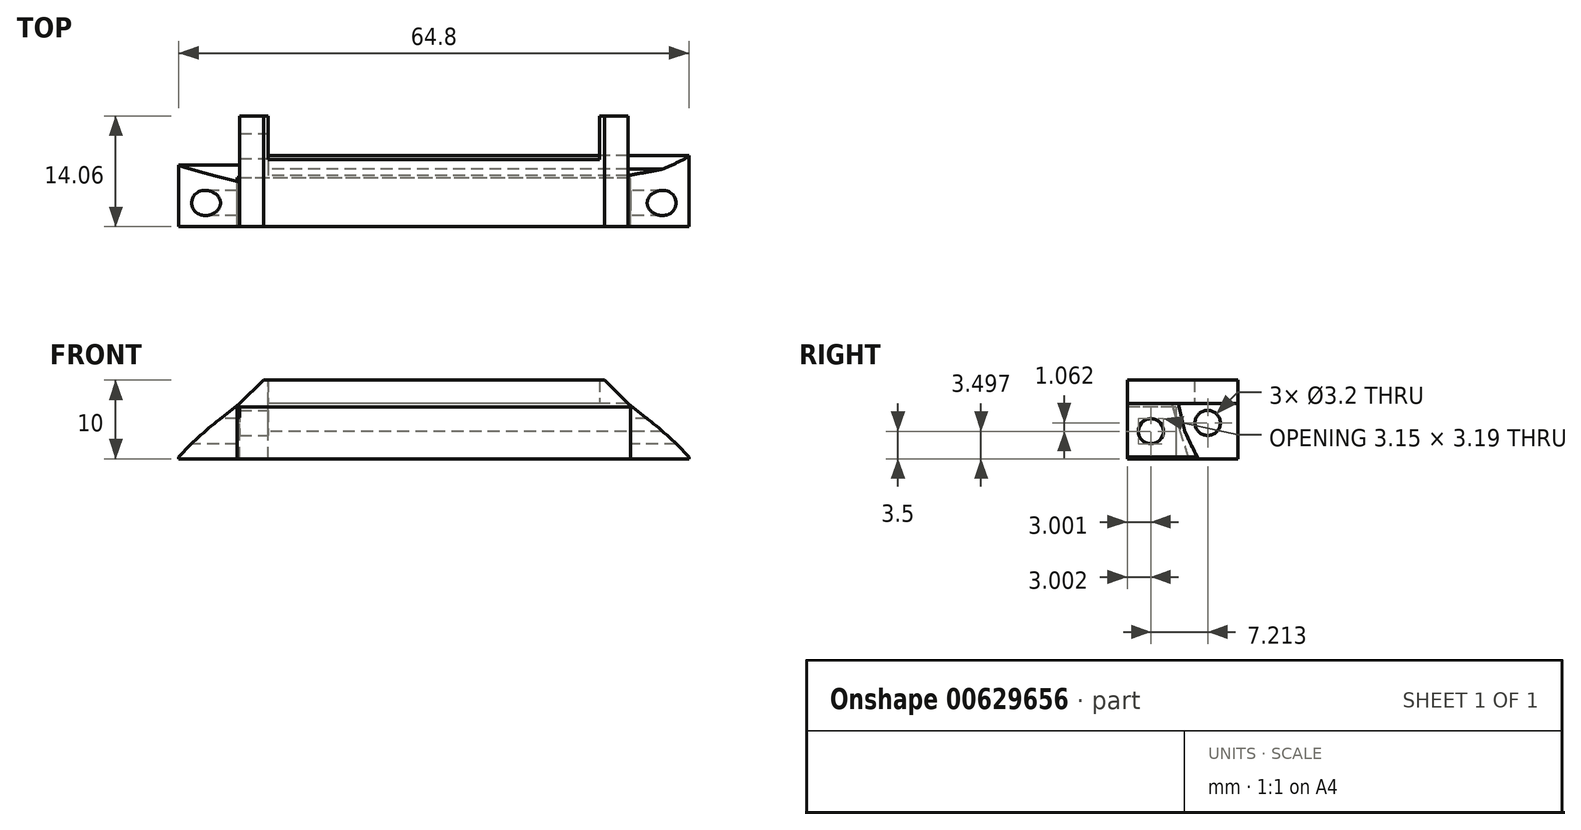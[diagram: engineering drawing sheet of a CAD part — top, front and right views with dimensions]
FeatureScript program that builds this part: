
annotation { "Feature Type Name" : "Feature", "Feature Type Description" : "" }
export const myFeature = defineFeature(function(context is Context, id is Id, definition is map)
    precondition{}
    {
        {
            var Q0;
            Q0=qCreatedBy(makeId("Right.planeOp"),FACE);
            cPlane(context, id + "F0", {"entities" : qUnion([Q0]), "cplaneType" : CPlaneType.OFFSET, "offset" : 40 * mm, "oppositeDirection" : true, "width" : 150 * mm, "height" : 150 * mm});
        }
        {
            var Q0;
            Q0=qCreatedBy(id+"F0.planeOp",FACE);
            var sketch = newSketch(context, id + "F1", { "sketchPlane" : qUnion([Q0])});
            skLineSegment(sketch, "E0.0", {"start": v(-62.06, 47) * mm, "end": v(-55.56, 47) * mm});
            skLineSegment(sketch, "E1.0", {"start": v(-62.06, 40) * mm, "end": v(-53.06, 40) * mm});
            skLineSegment(sketch, "E2", {"start": v(-62.06, 47) * mm, "end": v(-62.06, 40) * mm});
            skCircle(sketch, "E3", {"center": v(-59.06, 43.5) * mm, "radius": 1.6 * mm});
            skArc(sketch, "E4.0", {"start": v(-55.56, 47) * mm, "mid": v(-55.17, 45.25) * mm, "end": v(-54.76, 43.5) * mm});
            skArc(sketch, "E5.0", {"start": v(-53.06, 40) * mm, "mid": v(-53.92, 41.74) * mm, "end": v(-54.76, 43.5) * mm});
            skCircle(sketch, "E6", {"center": v(-59.06, 43.5) * mm, "radius": 3.25 * mm, "construction": true});
            skSolve(sketch);
        }
        {
            var Q0;
            Q0=qSketchRegion(id+"F1",true);
            extrude(context, id + "F2", {"entities" : qUnion([Q0]), "depth" : 33 * mm, "hasSecondDirection" : true, "secondDirectionOppositeDirection" : true, "secondDirectionDepth" : 33 * mm});
        }
        {
            var Q0;
            Q0=qCreatedBy(makeId("Front.planeOp"),FACE);
            var sketch = newSketch(context, id + "F3", { "sketchPlane" : qUnion([Q0])});
            skLineSegment(sketch, "E7", {"start": v(-40, 73.73) * mm, "end": v(-40, 20.27) * mm, "construction": true});
            skLineSegment(sketch, "E8.MirrorCS", {"start": v(-67.23, 45) * mm, "end": v(-64.65, 47) * mm});
            skArc(sketch, "E9.MirrorCS", {"start": v(-72.4, 40.2) * mm, "mid": v(-69.92, 42.72) * mm, "end": v(-67.23, 45) * mm});
            skLineSegment(sketch, "E10", {"start": v(-64.65, 47) * mm, "end": v(-77.52, 47) * mm});
            skLineSegment(sketch, "E11", {"start": v(-77.52, 47) * mm, "end": v(-77.52, 39.44) * mm});
            skLineSegment(sketch, "E12", {"start": v(-77.52, 39.44) * mm, "end": v(-72.4, 39.44) * mm});
            skLineSegment(sketch, "E13", {"start": v(-72.4, 39.44) * mm, "end": v(-72.4, 40.2) * mm});
            skLineSegment(sketch, "E14.MirrorCS", {"start": v(-7.6, 39.44) * mm, "end": v(-7.6, 40.2) * mm});
            skLineSegment(sketch, "E15.MirrorCS", {"start": v(-12.77, 45) * mm, "end": v(-15.35, 47) * mm});
            skLineSegment(sketch, "E16.MirrorCS", {"start": v(-2.48, 39.44) * mm, "end": v(-7.6, 39.44) * mm});
            skLineSegment(sketch, "E17.MirrorCS", {"start": v(-2.48, 47) * mm, "end": v(-2.48, 39.44) * mm});
            skArc(sketch, "E18.MirrorCS", {"start": v(-7.6, 40.2) * mm, "mid": v(-10.08, 42.72) * mm, "end": v(-12.77, 45) * mm});
            skLineSegment(sketch, "E19.MirrorCS", {"start": v(-15.35, 47) * mm, "end": v(-2.48, 47) * mm});
            skSolve(sketch);
        }
        {
            var Q0;
            Q0=qSketchRegion(id+"F3",true);
            extrude(context, id + "F4", {"entities" : qUnion([Q0]), "operationType" : NewBodyOperationType.REMOVE, "endBound" : BoundingType.THROUGH_ALL, "depth" : 25 * mm});
        }
        {
            var Q0;
            Q0=qCreatedBy(makeId("Front.planeOp"),FACE);
            cPlane(context, id + "F5", {"entities" : qUnion([Q0]), "cplaneType" : CPlaneType.OFFSET, "offset" : 48 * mm, "width" : 150 * mm, "height" : 150 * mm});
        }
        {
            var Q0;
            Q0=qCreatedBy(id+"F5.planeOp",FACE);
            var sketch = newSketch(context, id + "F6", { "sketchPlane" : qUnion([Q0])});
            skCircle(sketch, "E20", {"center": v(-62.85, 44.9) * mm, "radius": 1.8 * mm, "construction": true});
            skLineSegment(sketch, "E21", {"start": v(-64.65, 44.9) * mm, "end": v(-64.65, 47) * mm});
            skLineSegment(sketch, "E22", {"start": v(-64.65, 44.9) * mm, "end": v(-64.65, 40) * mm});
            skLineSegment(sketch, "E23", {"start": v(-62.85, 50.35) * mm, "end": v(-62.85, 37.67) * mm, "construction": true});
            skLineSegment(sketch, "E24.MirrorCS", {"start": v(-61.05, 44.9) * mm, "end": v(-61.05, 47) * mm});
            skLineSegment(sketch, "E25.MirrorCS", {"start": v(-61.05, 44.9) * mm, "end": v(-61.05, 40) * mm});
            skLineSegment(sketch, "E26", {"start": v(-61.05, 47) * mm, "end": v(-64.65, 47) * mm});
            skLineSegment(sketch, "E27", {"start": v(-64.65, 40) * mm, "end": v(-61.05, 40) * mm});
            skSolve(sketch);
        }
        {
            var Q0;
            Q0=qSketchRegion(id+"F6",true);
            extrude(context, id + "F7", {"entities" : qUnion([Q0]), "operationType" : NewBodyOperationType.ADD, "endBound" : BoundingType.UP_TO_NEXT, "depth" : 25 * mm});
        }
        {
            var Q0;
            Q0=qCreatedBy(id+"F0.planeOp",FACE);
            var sketch = newSketch(context, id + "F8", { "sketchPlane" : qUnion([Q0])});
            skLineSegment(sketch, "E28.bottom", {"start": v(-55.86, 46.6) * mm, "end": v(-62.16, 46.6) * mm});
            skLineSegment(sketch, "E28.top", {"start": v(-55.86, 39.6) * mm, "end": v(-62.16, 39.6) * mm});
            skLineSegment(sketch, "E28.left", {"start": v(-55.86, 46.6) * mm, "end": v(-55.86, 39.6) * mm});
            skLineSegment(sketch, "E28.right", {"start": v(-62.16, 46.6) * mm, "end": v(-62.16, 39.6) * mm});
            skSolve(sketch);
        }
        {
            var Q0;
            Q0=qSketchRegion(id+"F8",true);
            extrude(context, id + "F9", {"entities" : qUnion([Q0]), "operationType" : NewBodyOperationType.REMOVE, "oppositeDirection" : true, "depth" : 25 * mm, "hasSecondDirection" : true, "secondDirectionOppositeDirection" : false, "secondDirectionDepth" : 25 * mm});
        }
        {
            var Q0;
            Q0=qCreatedBy(id+"F0.planeOp",FACE);
            var sketch = newSketch(context, id + "F10", { "sketchPlane" : qUnion([Q0])});
            skCircle(sketch, "E29", {"center": v(-51.84, 44.56) * mm, "radius": 1.6 * mm});
            skSolve(sketch);
        }
        {
            var Q0;
            Q0=qSketchRegion(id+"F10",true);
            extrude(context, id + "F11", {"entities" : qUnion([Q0]), "operationType" : NewBodyOperationType.REMOVE, "endBound" : BoundingType.THROUGH_ALL, "oppositeDirection" : true, "depth" : 25 * mm, "hasSecondDirection" : true, "secondDirectionBound" : SecondDirectionBoundingType.THROUGH_ALL, "secondDirectionOppositeDirection" : false, "secondDirectionDepth" : 25 * mm});
        }
        {
            var Q0;
            {var subQ0=sQuery(id+"F6.wireOp",EDGE,"E26");Q0=makeQuery(id+"FYnT0MVXlafkFCY_3.1.F7.boolean.opBoolean","MERGE",FACE,{"derivedFrom":[makeQuery(id+"F7.boolean.opBoolean","MERGE",FACE,{"derivedFrom":[makeQuery(id+"F2.opExtrude","SWEPT_FACE",FACE,{"disambiguationData":[OSD([sQuery(id+"F1.wireOp",EDGE,"E0.0")])]}),makeQuery(id+"F7.opExtrude","SWEPT_FACE",FACE,{"disambiguationData":[OSD([subQ0])]})]}),makeQuery(id+"FYnT0MVXlafkFCY_3.1.F7.opExtrude","SWEPT_FACE",FACE,{"disambiguationData":[OSD([subQ0])]})]});}
            var sketch = newSketch(context, id + "F12", { "sketchPlane" : qUnion([Q0])});
            skLineSegment(sketch, "E30.0.0", {"start": v(-64.65, -55.56) * mm, "end": v(-64.65, -62.06) * mm});
            skLineSegment(sketch, "E30.0.1", {"start": v(-64.65, -62.06) * mm, "end": v(-15.35, -62.06) * mm});
            skLineSegment(sketch, "E30.0.2", {"start": v(-15.35, -62.06) * mm, "end": v(-15.35, -55.56) * mm});
            skLineSegment(sketch, "E30.0.3", {"start": v(-15.35, -55.56) * mm, "end": v(-15.35, -48) * mm});
            skLineSegment(sketch, "E30.0.4", {"start": v(-15.35, -48) * mm, "end": v(-18.95, -48) * mm});
            skLineSegment(sketch, "E30.0.5", {"start": v(-18.95, -48) * mm, "end": v(-18.95, -55.56) * mm});
            skLineSegment(sketch, "E30.0.6", {"start": v(-18.95, -55.56) * mm, "end": v(-61.05, -55.56) * mm});
            skLineSegment(sketch, "E30.0.7", {"start": v(-61.05, -55.56) * mm, "end": v(-61.05, -48) * mm});
            skLineSegment(sketch, "E30.0.8", {"start": v(-61.05, -48) * mm, "end": v(-64.65, -48) * mm});
            skLineSegment(sketch, "E30.0.9", {"start": v(-64.65, -48) * mm, "end": v(-64.65, -55.56) * mm});
            skSolve(sketch);
        }
        {
            var Q0;
            Q0=qSketchRegion(id+"F12",true);
            extrude(context, id + "F13", {"entities" : qUnion([Q0]), "operationType" : NewBodyOperationType.ADD, "depth" : 3 * mm});
        }
        {
            var Q0;
            Q0=makeQuery(id+"F13.opExtrude","SWEPT_FACE",FACE,{"disambiguationData":[OSD([sQuery(id+"F12.wireOp",EDGE,"E30.0.6")])]});
            var sketch = newSketch(context, id + "F14", { "sketchPlane" : qUnion([Q0])});
            skLineSegment(sketch, "E31.0.0", {"start": v(18.95, 47) * mm, "end": v(61.05, 47) * mm});
            skLineSegment(sketch, "E31.0.1", {"start": v(61.05, 47) * mm, "end": v(61.05, 50) * mm});
            skLineSegment(sketch, "E31.0.2", {"start": v(61.05, 50) * mm, "end": v(18.95, 50) * mm});
            skLineSegment(sketch, "E31.0.3", {"start": v(18.95, 50) * mm, "end": v(18.95, 47) * mm});
            skSolve(sketch);
        }
        {
            var Q0;
            Q0=qSketchRegion(id+"F14",true);
            extrude(context, id + "F15", {"entities" : qUnion([Q0]), "operationType" : NewBodyOperationType.ADD, "depth" : 2 * mm});
        }
        {
            var Q0;
            Q0=makeQuery(id+"F13.opExtrude","CAP_EDGE",EDGE,{"disambiguationData":[OSD([sQuery(id+"F12.wireOp",EDGE,"E30.0.0"),sQuery(id+"F12.wireOp",EDGE,"E30.0.9")])],"isStart":false});
            var Q1;
            Q1=makeQuery(id+"F13.opExtrude","CAP_EDGE",EDGE,{"disambiguationData":[OSD([sQuery(id+"F12.wireOp",EDGE,"E30.0.2"),sQuery(id+"F12.wireOp",EDGE,"E30.0.3")])],"isStart":false});
            chamfer(context, id + "F16", {"entities" : qUnion([Q0, Q1]), "width" : 3 * mm, "tangentPropagation" : true});
        }
        {
            var Q0;
            Q0=makeQuery(id+"F13.boolean.opBoolean","MERGE",FACE,{"derivedFrom":[makeQuery(id+"F7.opExtrude","SWEPT_FACE",FACE,{"disambiguationData":[OSD([sQuery(id+"F6.wireOp",EDGE,"E21"),sQuery(id+"F6.wireOp",EDGE,"E22")])]}),makeQuery(id+"F13.opExtrude","SWEPT_FACE",FACE,{"disambiguationData":[OSD([sQuery(id+"F12.wireOp",EDGE,"E30.0.0"),sQuery(id+"F12.wireOp",EDGE,"E30.0.9")])]})]});
            var sketch = newSketch(context, id + "F17", { "sketchPlane" : qUnion([Q0])});
            skLineSegment(sketch, "E32", {"start": v(55.56, 47) * mm, "end": v(53.06, 40) * mm});
            skLineSegment(sketch, "E33", {"start": v(53.06, 40) * mm, "end": v(54.22, 40) * mm});
            skLineSegment(sketch, "E34", {"start": v(54.22, 40) * mm, "end": v(56.4, 47) * mm});
            skLineSegment(sketch, "E35", {"start": v(56.4, 47) * mm, "end": v(55.56, 47) * mm});
            skSolve(sketch);
        }
        {
            var Q0;
            Q0=qSketchRegion(id+"F17",true);
            extrude(context, id + "F18", {"entities" : qUnion([Q0]), "operationType" : NewBodyOperationType.REMOVE, "depth" : 25 * mm});
        }
    });
